# Revit family: 265-91-001 DN450-600
name_source: partatom
category: Pipe Accessories
units: mm (PartAtom-declared; Revit-internal decimal feet)

## family parameters
Always vertical = Yes
Cut with Voids When Loaded = No
Part Type = Valve - Breaks Into
Round Connector Dimension = Use Diameter
Shared = No
Work Plane-Based = No

## types (6) — shared parameters
25 = 25 mm  [stored 0.082021 ft]
Bolt.no = 20 mm  [stored 0.0656168 ft]
DN450_PN10 = 265-9-0450-11-04036401
DN450_PN16 = 265-9-0450-10-14036400
265-9-0450-10-14036400
265-9-0450-10-14036400
DN500_PN10 = 265-9-0500-11-04036401
DN500_PN16 = 265-9-0500-10-14036400
DN600_PN10 = 265-9-0600-11-04036401
DN600_PN16 = 265-9-0600-10-14036400
Description_ = AVK DISMANTLING JOINT WITH CENTRE FLANGE, PN10/16
Search_table = 265-91-001 DN450-600
URL_product_pages = https://www.avkvalves.com
zero-valued in all types: Default Elevation

## per-type parameters (varying)
| type | B1 | Bore | D | DN | FL_T | FL_T/2 | L | L1 | L11 | L2 | L3 | Nut_T | PCD | PN | Raised_dis | S | S11 | T | T1 | offset | raised_R |
| DN500_PN10 | 32 mm  [stored 0.104987 ft] | 250 mm  [stored 0.82021 ft] | 335 mm | 500 mm | 30 mm  [stored 0.0984252 ft] | 15 mm  [stored 0.0492126 ft] | 405 mm | 177 mm | 260 mm  [stored 0.853018 ft] | 26 mm | 15 mm  [stored 0.0492126 ft] | 23 mm | 310 mm | 10 mm  [stored 0.0328084 ft] | 4 mm  [stored 0.0131234 ft] | 24 mm  [stored 0.0787402 ft] | 32 mm  [stored 0.104987 ft] | 9 mm  [stored 0.0295276 ft] | 23 mm | 8 mm  [stored 0.0262467 ft] | 268 mm |
| DN500_PN16 | 37 mm | 250 mm  [stored 0.82021 ft] | 358 mm | 500 mm | 32 mm  [stored 0.104987 ft] | 16 mm  [stored 0.0524934 ft] | 460 mm | 190 mm | 280 mm | 30 mm  [stored 0.0984252 ft] | 16 mm  [stored 0.0524934 ft] | 24 mm  [stored 0.0787402 ft] | 325 mm | 16 mm  [stored 0.0524934 ft] | 4 mm  [stored 0.0131234 ft] | 30 mm  [stored 0.0984252 ft] | 41 mm | 9 mm  [stored 0.0295276 ft] | 24 mm  [stored 0.0787402 ft] | 11 mm | 286 mm |
| DN450_PN10 | 32 mm  [stored 0.104987 ft] | 225 mm  [stored 0.738189 ft] | 308 mm | 450 mm | 27 mm  [stored 0.0885827 ft] | 13 mm  [stored 0.0426509 ft] | 405 mm | 170 mm  [stored 0.557743 ft] | 250 mm  [stored 0.82021 ft] | 26 mm | 13 mm  [stored 0.0426509 ft] | 20 mm  [stored 0.0656168 ft] | 283 mm | 10 mm  [stored 0.0328084 ft] | 4 mm  [stored 0.0131234 ft] | 24 mm  [stored 0.0787402 ft] | 32 mm  [stored 0.104987 ft] | 8 mm  [stored 0.0262467 ft] | 20 mm  [stored 0.0656168 ft] | 8 mm  [stored 0.0262467 ft] | 246 mm  [stored 0.807087 ft] |
| DN450_PN16 | 35 mm  [stored 0.114829 ft] | 225 mm  [stored 0.738189 ft] | 320 mm | 450 mm | 30 mm  [stored 0.0984252 ft] | 15 mm  [stored 0.0492126 ft] | 440 mm | 184 mm | 270 mm | 29 mm | 15 mm  [stored 0.0492126 ft] | 23 mm | 293 mm | 16 mm  [stored 0.0524934 ft] | 4 mm  [stored 0.0131234 ft] | 27 mm  [stored 0.0885827 ft] | 36 mm  [stored 0.11811 ft] | 9 mm  [stored 0.0295276 ft] | 23 mm | 9 mm  [stored 0.0295276 ft] | 256 mm  [stored 0.839895 ft] |
| DN600_PN16 | 40 mm  [stored 0.131234 ft] | 300 mm | 420 mm | 600 mm | 36 mm  [stored 0.11811 ft] | 18 mm  [stored 0.0590551 ft] | 500 mm | 204 mm | 300 mm | 33 mm  [stored 0.108268 ft] | 18 mm  [stored 0.0590551 ft] | 27 mm  [stored 0.0885827 ft] | 385 mm | 16 mm  [stored 0.0524934 ft] | 5 mm  [stored 0.0164042 ft] | 33 mm  [stored 0.108268 ft] | 45 mm  [stored 0.147638 ft] | 11 mm | 27 mm  [stored 0.0885827 ft] | 12 mm  [stored 0.0393701 ft] | 336 mm |
| DN600_PN10 | 34 mm | 300 mm | 390 mm | 600 mm | 33 mm  [stored 0.108268 ft] | 16 mm  [stored 0.0524934 ft] | 430 mm | 177 mm | 260 mm  [stored 0.853018 ft] | 28 mm  [stored 0.0918635 ft] | 16 mm  [stored 0.0524934 ft] | 24 mm  [stored 0.0787402 ft] | 363 mm | 10 mm  [stored 0.0328084 ft] | 5 mm  [stored 0.0164042 ft] | 27 mm  [stored 0.0885827 ft] | 36 mm  [stored 0.11811 ft] | 10 mm  [stored 0.0328084 ft] | 24 mm  [stored 0.0787402 ft] | 9 mm  [stored 0.0295276 ft] | 312 mm |

note: [stored X ft] marks values corroborated as IEEE doubles in the binary element streams (Revit-internal decimal feet)

## geometry (parser evidence)
native form markers: Sweep x11
no freeform markers — native parametric forms only
